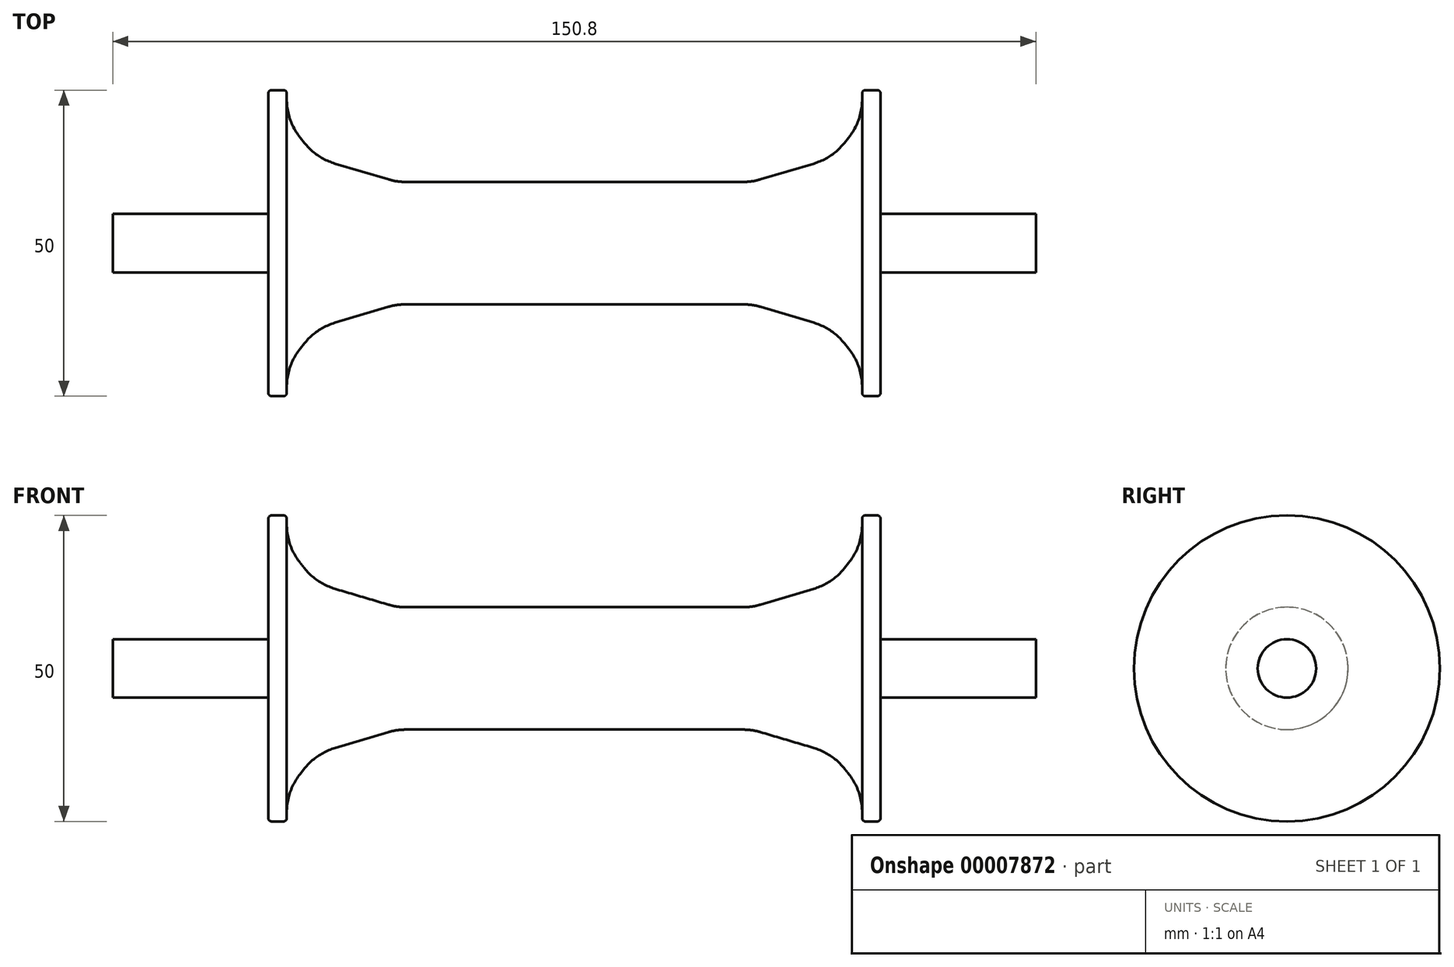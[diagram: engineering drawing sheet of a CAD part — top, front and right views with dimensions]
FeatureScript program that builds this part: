
annotation { "Feature Type Name" : "Feature", "Feature Type Description" : "" }
export const myFeature = defineFeature(function(context is Context, id is Id, definition is map)
    precondition{}
    {
        {
            var Q0;
            Q0=qCreatedBy(makeId("Front.planeOp"),FACE);
            var sketch = newSketch(context, id + "F0", { "sketchPlane" : qUnion([Q0])});
            skLineSegment(sketch, "E0", {"start": v(-50, 0) * mm, "end": v(50, 0) * mm});
            skLineSegment(sketch, "E1", {"start": v(-50, 0) * mm, "end": v(-50, 25) * mm});
            skLineSegment(sketch, "E2", {"start": v(-50, 25) * mm, "end": v(-47, 25) * mm});
            skLineSegment(sketch, "E3", {"start": v(-47, 25) * mm, "end": v(-47, 10) * mm});
            skLineSegment(sketch, "E4", {"start": v(-47, 10) * mm, "end": v(47, 10) * mm});
            skLineSegment(sketch, "E5", {"start": v(47, 10) * mm, "end": v(47, 25) * mm});
            skLineSegment(sketch, "E6", {"start": v(47, 25) * mm, "end": v(50, 25) * mm});
            skLineSegment(sketch, "E7", {"start": v(50, 25) * mm, "end": v(50, 0) * mm});
            skSolve(sketch);
        }
        {
            var Q0;
            Q0 = qSketchRegion(id + "F0", true);
            var Q1;
            Q1=sQuery(id+"F0.wireOp",EDGE,"E0");
            revolve(context, id + "F1", {"entities" : qUnion([Q0]), "axis" : qUnion([Q1]), "revolveType" : RevolveType.FULL});
        }
        {
            var Q0;
            Q0=makeQuery(id+"F1.opRevolve","SWEPT_EDGE",EDGE,{"disambiguationData":[OSD([sQuery(id+"F0.wireOp",EDGE,"E3"),sQuery(id+"F0.wireOp",EDGE,"E4")])]});
            var Q1;
            Q1=makeQuery(id+"F1.opRevolve","SWEPT_EDGE",EDGE,{"disambiguationData":[OSD([sQuery(id+"F0.wireOp",EDGE,"E4"),sQuery(id+"F0.wireOp",EDGE,"E5")])]});
            chamfer(context, id + "F2", {"entities" : qUnion([Q0, Q1]), "chamferType" : ChamferType.TWO_OFFSETS, "width1" : 10 * mm, "oppositeDirection" : false, "width2" : 8 * mm, "tangentPropagation" : true});
        }
        {
            var Q0;
            {var subQ0=sQuery(id+"F0.wireOp",EDGE,"E4");Q0=makeQuery(id+"F2.opChamfer","BLEND_EDGE",EDGE,{"blendedFrom":[makeQuery(id+"F1.opRevolve","SWEPT_EDGE",EDGE,{"disambiguationData":[OSD([sQuery(id+"F0.wireOp",EDGE,"E3"),subQ0])]}),makeQuery(id+"F1.opRevolve","SWEPT_FACE",FACE,{"disambiguationData":[OSD([subQ0])]})],"blendedInto":[makeQuery(id+"F1.opRevolve","SWEPT_FACE",FACE,{"disambiguationData":[OSD([subQ0])]})]});}
            var Q1;
            {var subQ0=sQuery(id+"F0.wireOp",EDGE,"E4");Q1=makeQuery(id+"F2.opChamfer","BLEND_EDGE",EDGE,{"blendedFrom":[makeQuery(id+"F1.opRevolve","SWEPT_EDGE",EDGE,{"disambiguationData":[OSD([subQ0,sQuery(id+"F0.wireOp",EDGE,"E5")])]}),makeQuery(id+"F1.opRevolve","SWEPT_FACE",FACE,{"disambiguationData":[OSD([subQ0])]})],"blendedInto":[makeQuery(id+"F1.opRevolve","SWEPT_FACE",FACE,{"disambiguationData":[OSD([subQ0])]})]});}
            chamfer(context, id + "F3", {"entities" : qUnion([Q0, Q1]), "chamferType" : ChamferType.TWO_OFFSETS, "width1" : 10 * mm, "oppositeDirection" : false, "width2" : 5 * mm, "tangentPropagation" : true});
        }
        {
            var Q0;
            {var subQ0=sQuery(id+"F0.wireOp",EDGE,"E3");Q0=makeQuery(id+"F2.opChamfer","BLEND_EDGE",EDGE,{"blendedFrom":[makeQuery(id+"F1.opRevolve","SWEPT_EDGE",EDGE,{"disambiguationData":[OSD([subQ0,sQuery(id+"F0.wireOp",EDGE,"E4")])]}),makeQuery(id+"F1.opRevolve","SWEPT_FACE",FACE,{"disambiguationData":[OSD([subQ0])]})],"blendedInto":[makeQuery(id+"F1.opRevolve","SWEPT_FACE",FACE,{"disambiguationData":[OSD([subQ0])]})]});}
            var Q1;
            {var subQ0=sQuery(id+"F0.wireOp",EDGE,"E3");var subQ1=sQuery(id+"F0.wireOp",EDGE,"E4");Q1=makeQuery(id+"F3.opChamfer","BLEND_EDGE",EDGE,{"blendedFrom":[makeQuery(id+"F2.opChamfer","BLEND_EDGE",EDGE,{"blendedFrom":[makeQuery(id+"F1.opRevolve","SWEPT_EDGE",EDGE,{"disambiguationData":[OSD([subQ0,subQ1])]}),makeQuery(id+"F1.opRevolve","SWEPT_FACE",FACE,{"disambiguationData":[OSD([subQ1])]})],"blendedInto":[makeQuery(id+"F1.opRevolve","SWEPT_FACE",FACE,{"disambiguationData":[OSD([subQ1])]})]}),makeQuery(id+"F2.opChamfer","BLEND_FACE",FACE,{"disambiguationData":[OSD([subQ0,subQ1])]})],"blendedInto":[makeQuery(id+"F2.opChamfer","BLEND_FACE",FACE,{"disambiguationData":[OSD([subQ0,subQ1])]})]});}
            var Q2;
            {var subQ0=sQuery(id+"F0.wireOp",EDGE,"E4");var subQ1=makeQuery(id+"F1.opRevolve","SWEPT_FACE",FACE,{"disambiguationData":[OSD([subQ0])]});Q2=makeQuery(id+"F3.opChamfer","BLEND_EDGE",EDGE,{"blendedFrom":[makeQuery(id+"F2.opChamfer","BLEND_EDGE",EDGE,{"blendedFrom":[makeQuery(id+"F1.opRevolve","SWEPT_EDGE",EDGE,{"disambiguationData":[OSD([sQuery(id+"F0.wireOp",EDGE,"E3"),subQ0])]}),subQ1],"blendedInto":[subQ1]}),subQ1],"blendedInto":[subQ1]});}
            var Q3;
            {var subQ0=sQuery(id+"F0.wireOp",EDGE,"E4");var subQ1=makeQuery(id+"F1.opRevolve","SWEPT_FACE",FACE,{"disambiguationData":[OSD([subQ0])]});Q3=makeQuery(id+"F3.opChamfer","BLEND_EDGE",EDGE,{"blendedFrom":[makeQuery(id+"F2.opChamfer","BLEND_EDGE",EDGE,{"blendedFrom":[makeQuery(id+"F1.opRevolve","SWEPT_EDGE",EDGE,{"disambiguationData":[OSD([subQ0,sQuery(id+"F0.wireOp",EDGE,"E5")])]}),subQ1],"blendedInto":[subQ1]}),subQ1],"blendedInto":[subQ1]});}
            var Q4;
            {var subQ0=sQuery(id+"F0.wireOp",EDGE,"E4");var subQ1=sQuery(id+"F0.wireOp",EDGE,"E5");Q4=makeQuery(id+"F3.opChamfer","BLEND_EDGE",EDGE,{"blendedFrom":[makeQuery(id+"F2.opChamfer","BLEND_EDGE",EDGE,{"blendedFrom":[makeQuery(id+"F1.opRevolve","SWEPT_EDGE",EDGE,{"disambiguationData":[OSD([subQ0,subQ1])]}),makeQuery(id+"F1.opRevolve","SWEPT_FACE",FACE,{"disambiguationData":[OSD([subQ0])]})],"blendedInto":[makeQuery(id+"F1.opRevolve","SWEPT_FACE",FACE,{"disambiguationData":[OSD([subQ0])]})]}),makeQuery(id+"F2.opChamfer","BLEND_FACE",FACE,{"disambiguationData":[OSD([subQ0,subQ1])]})],"blendedInto":[makeQuery(id+"F2.opChamfer","BLEND_FACE",FACE,{"disambiguationData":[OSD([subQ0,subQ1])]})]});}
            var Q5;
            {var subQ0=sQuery(id+"F0.wireOp",EDGE,"E5");Q5=makeQuery(id+"F2.opChamfer","BLEND_EDGE",EDGE,{"blendedFrom":[makeQuery(id+"F1.opRevolve","SWEPT_EDGE",EDGE,{"disambiguationData":[OSD([sQuery(id+"F0.wireOp",EDGE,"E4"),subQ0])]}),makeQuery(id+"F1.opRevolve","SWEPT_FACE",FACE,{"disambiguationData":[OSD([subQ0])]})],"blendedInto":[makeQuery(id+"F1.opRevolve","SWEPT_FACE",FACE,{"disambiguationData":[OSD([subQ0])]})]});}
            fillet(context, id + "F4", {"entities" : qUnion([Q0, Q1, Q2, Q3, Q4, Q5]), "radius" : 10 * mm, "tangentPropagation" : true, "allowEdgeOverflow" : false});
        }
        {
            var Q0;
            Q0=makeQuery(id+"F1.opRevolve","SWEPT_EDGE",EDGE,{"disambiguationData":[OSD([sQuery(id+"F0.wireOp",EDGE,"E1"),sQuery(id+"F0.wireOp",EDGE,"E2")])]});
            var Q1;
            Q1=makeQuery(id+"F1.opRevolve","SWEPT_EDGE",EDGE,{"disambiguationData":[OSD([sQuery(id+"F0.wireOp",EDGE,"E2"),sQuery(id+"F0.wireOp",EDGE,"E3")])]});
            var Q2;
            Q2=makeQuery(id+"F1.opRevolve","SWEPT_EDGE",EDGE,{"disambiguationData":[OSD([sQuery(id+"F0.wireOp",EDGE,"E5"),sQuery(id+"F0.wireOp",EDGE,"E6")])]});
            var Q3;
            Q3=makeQuery(id+"F1.opRevolve","SWEPT_EDGE",EDGE,{"disambiguationData":[OSD([sQuery(id+"F0.wireOp",EDGE,"E6"),sQuery(id+"F0.wireOp",EDGE,"E7")])]});
            fillet(context, id + "F5", {"entities" : qUnion([Q0, Q1, Q2, Q3]), "radius" : .5 * mm, "tangentPropagation" : true, "allowEdgeOverflow" : false});
        }
        {
            var Q0;
            Q0=makeQuery(id+"F1.opRevolve","SWEPT_FACE",FACE,{"disambiguationData":[OSD([sQuery(id+"F0.wireOp",EDGE,"E1")])]});
            var sketch = newSketch(context, id + "F6", { "sketchPlane" : qUnion([Q0])});
            skCircle(sketch, "E8", {"center": v(0, 0) * mm, "radius": 4.77 * mm});
            skSolve(sketch);
        }
        {
            var Q0;
            Q0 = qSketchRegion(id + "F6", true);
            extrude(context, id + "F7", {"entities" : qUnion([Q0]), "operationType" : NewBodyOperationType.ADD, "depth" : 25.4 * mm});
        }
        {
            var Q0;
            Q0=makeQuery(id+"F7.opExtrude","SWEPT_FACE",FACE,{"disambiguationData":[OSD([sQuery(id+"F6.wireOp",EDGE,"E8")])]});
            var Q1;
            Q1=makeQuery(id+"F7.opExtrude","CAP_FACE",FACE,{"disambiguationData":[OSD([sQuery(id+"F6.wireOp",EDGE,"E8")])],"isStart":false});
            var Q2;
            Q2=qCreatedBy(makeId("Right.planeOp"),FACE);
            mirror(context, id + "F8", {"faces" : qUnion([Q0, Q1]), "mirrorPlane" : qUnion([Q2]), "patternType" : MirrorType.FACE});
        }
    });
